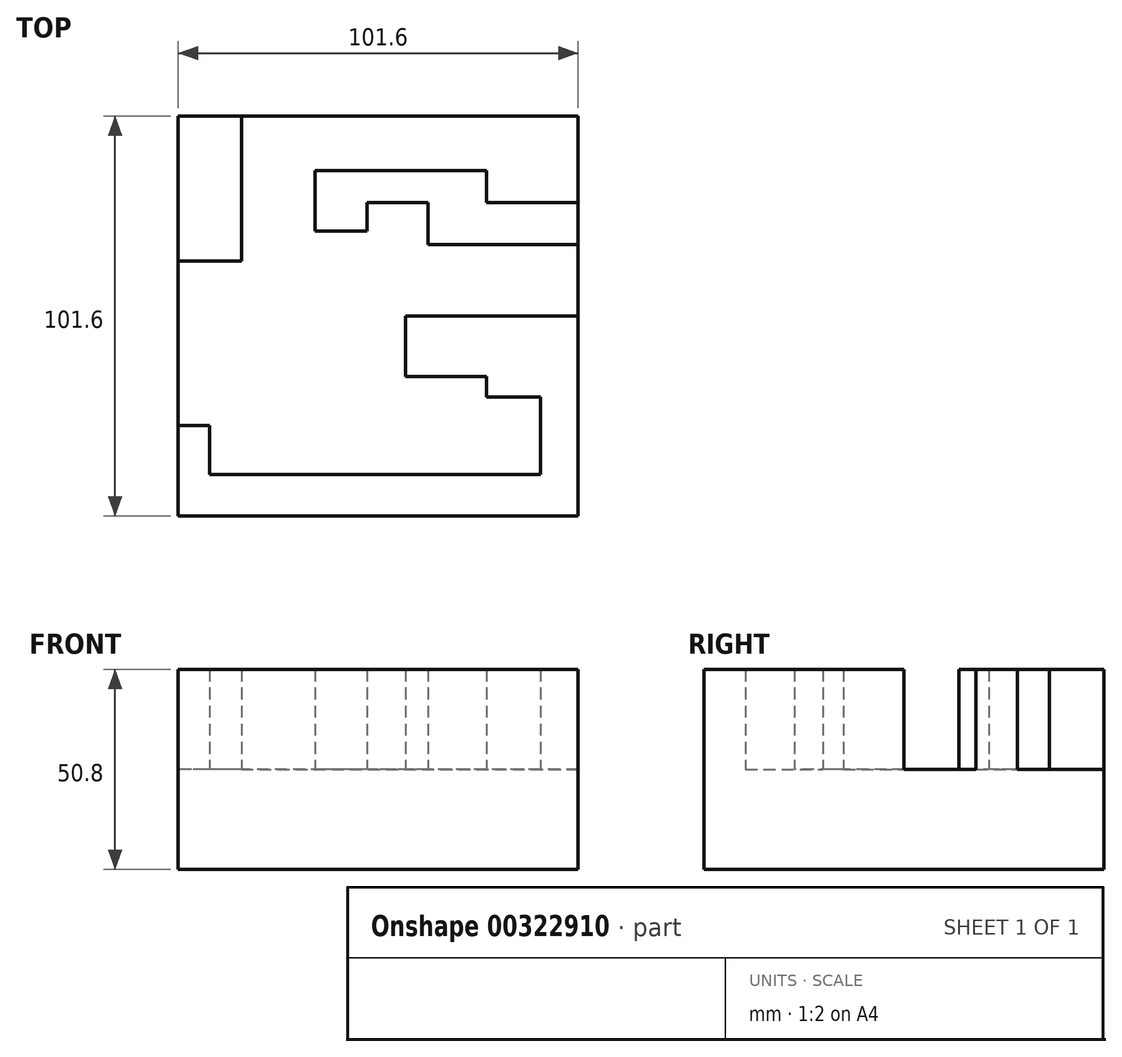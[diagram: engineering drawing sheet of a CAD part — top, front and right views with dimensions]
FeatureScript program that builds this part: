
annotation { "Feature Type Name" : "Feature", "Feature Type Description" : "" }
export const myFeature = defineFeature(function(context is Context, id is Id, definition is map)
    precondition{}
    {
        {
            var Q0;
            Q0=qCreatedBy(makeId("Top.planeOp"),FACE);
            var sketch = newSketch(context, id + "F0", { "sketchPlane" : qUnion([Q0])});
            skLineSegment(sketch, "E0.bottom", {"start": v(-47.92, 62.04) * mm, "end": v(53.68, 62.04) * mm});
            skLineSegment(sketch, "E0.top", {"start": v(-47.92, -39.56) * mm, "end": v(53.68, -39.56) * mm});
            skLineSegment(sketch, "E0.left", {"start": v(-47.92, 62.04) * mm, "end": v(-47.92, -39.56) * mm});
            skLineSegment(sketch, "E0.right", {"start": v(53.68, 62.04) * mm, "end": v(53.68, -39.56) * mm});
            skSolve(sketch);
        }
        {
            var Q0;
            Q0=makeQuery(id+"F0.imprint","IMPRINT",FACE,{"disambiguationData":[TD([[makeQuery(id+"F0.imprint","IMPRINT",EDGE,{"derivedFrom":sQuery(id+"F0.wireOp",EDGE,"E0.bottom")}),-1.0]])]});
            extrude(context, id + "F1", {"entities" : qUnion([Q0]), "depth" : 25.4 * mm});
        }
        {
            var Q0;
            Q0=makeQuery(id+"F1.opExtrude","CAP_FACE",FACE,{"disambiguationData":[OSD([sQuery(id+"F0.wireOp",EDGE,"E0.bottom"),sQuery(id+"F0.wireOp",EDGE,"E0.top"),sQuery(id+"F0.wireOp",EDGE,"E0.left"),sQuery(id+"F0.wireOp",EDGE,"E0.right")])],"isStart":false});
            var sketch = newSketch(context, id + "F2", { "sketchPlane" : qUnion([Q0])});
            skLineSegment(sketch, "E1.bottom", {"start": v(53.68, -29.03) * mm, "end": v(-8.4, -29.03) * mm});
            skLineSegment(sketch, "E1.top", {"start": v(53.68, -39.56) * mm, "end": v(-8.4, -39.56) * mm});
            skLineSegment(sketch, "E1.left", {"start": v(53.68, -29.03) * mm, "end": v(53.68, -39.56) * mm});
            skLineSegment(sketch, "E1.right", {"start": v(-8.4, -29.03) * mm, "end": v(-8.4, -39.56) * mm});
            skLineSegment(sketch, "E2.bottom", {"start": v(53.68, 29.46) * mm, "end": v(15.58, 29.46) * mm});
            skLineSegment(sketch, "E2.top", {"start": v(53.68, 40) * mm, "end": v(15.58, 40) * mm});
            skLineSegment(sketch, "E2.left", {"start": v(53.68, 29.46) * mm, "end": v(53.68, 40) * mm});
            skLineSegment(sketch, "E2.right", {"start": v(15.58, 29.46) * mm, "end": v(15.58, 40) * mm});
            skLineSegment(sketch, "E3.bottom", {"start": v(-31.88, 62.04) * mm, "end": v(-47.92, 62.04) * mm});
            skLineSegment(sketch, "E3.top", {"start": v(-31.88, 25.15) * mm, "end": v(-47.92, 25.15) * mm});
            skLineSegment(sketch, "E3.left", {"start": v(-31.88, 62.04) * mm, "end": v(-31.88, 25.15) * mm});
            skLineSegment(sketch, "E3.right", {"start": v(-47.92, 62.04) * mm, "end": v(-47.92, 25.15) * mm});
            skLineSegment(sketch, "E4.bottom", {"start": v(30.45, 40) * mm, "end": v(0, 40) * mm});
            skLineSegment(sketch, "E4.top", {"start": v(30.45, 48.16) * mm, "end": v(0, 48.16) * mm});
            skLineSegment(sketch, "E4.left", {"start": v(30.45, 40) * mm, "end": v(30.45, 48.16) * mm});
            skLineSegment(sketch, "E4.right", {"start": v(0, 40) * mm, "end": v(0, 48.16) * mm});
            skLineSegment(sketch, "E5.bottom", {"start": v(0, 48.16) * mm, "end": v(-13.18, 48.16) * mm});
            skLineSegment(sketch, "E5.top", {"start": v(0, 32.82) * mm, "end": v(-13.18, 32.82) * mm});
            skLineSegment(sketch, "E5.left", {"start": v(0, 48.16) * mm, "end": v(0, 32.82) * mm});
            skLineSegment(sketch, "E5.right", {"start": v(-13.18, 48.16) * mm, "end": v(-13.18, 32.82) * mm});
            skLineSegment(sketch, "E6.bottom", {"start": v(-39.9, 25.15) * mm, "end": v(-47.92, 25.15) * mm});
            skLineSegment(sketch, "E6.top", {"start": v(-39.9, -16.57) * mm, "end": v(-47.92, -16.57) * mm});
            skLineSegment(sketch, "E6.left", {"start": v(-39.9, 25.15) * mm, "end": v(-39.9, -16.57) * mm});
            skLineSegment(sketch, "E6.right", {"start": v(-47.92, 25.15) * mm, "end": v(-47.92, -16.57) * mm});
            skLineSegment(sketch, "E7.bottom", {"start": v(-31.88, -39.56) * mm, "end": v(-47.92, -39.56) * mm});
            skLineSegment(sketch, "E7.top", {"start": v(-31.88, -29.03) * mm, "end": v(-47.92, -29.03) * mm});
            skLineSegment(sketch, "E7.left", {"start": v(-31.88, -39.56) * mm, "end": v(-31.88, -29.03) * mm});
            skLineSegment(sketch, "E7.right", {"start": v(-47.92, -39.56) * mm, "end": v(-47.92, -29.03) * mm});
            skLineSegment(sketch, "E8.bottom", {"start": v(53.68, 11.24) * mm, "end": v(30.45, 11.24) * mm});
            skLineSegment(sketch, "E8.top", {"start": v(53.68, -9.37) * mm, "end": v(30.45, -9.37) * mm});
            skLineSegment(sketch, "E8.left", {"start": v(53.68, 11.24) * mm, "end": v(53.68, -9.37) * mm});
            skLineSegment(sketch, "E8.right", {"start": v(30.45, 11.24) * mm, "end": v(30.45, -9.37) * mm});
            skLineSegment(sketch, "E9.bottom", {"start": v(30.45, -4.1) * mm, "end": v(9.83, -4.1) * mm});
            skLineSegment(sketch, "E9.top", {"start": v(30.45, 11.24) * mm, "end": v(9.83, 11.24) * mm});
            skLineSegment(sketch, "E9.left", {"start": v(30.45, -4.1) * mm, "end": v(30.45, 11.24) * mm});
            skLineSegment(sketch, "E9.right", {"start": v(9.83, -4.1) * mm, "end": v(9.83, 11.24) * mm});
            skLineSegment(sketch, "E10.bottom", {"start": v(44.07, -29.03) * mm, "end": v(42.06, -29.03) * mm});
            skLineSegment(sketch, "E10.top", {"start": v(44.07, -9.37) * mm, "end": v(42.06, -9.37) * mm});
            skLineSegment(sketch, "E10.left", {"start": v(44.07, -29.03) * mm, "end": v(44.07, -9.37) * mm});
            skLineSegment(sketch, "E10.right", {"start": v(42.06, -29.03) * mm, "end": v(42.06, -9.37) * mm});
            skPoint(sketch, "E11.oppositeSnap0", {"position": v(42.06, 11.24) * mm});
            skLineSegment(sketch, "E11.bottom", {"start": v(42.06, 11.24) * mm, "end": v(42.06, 11.24) * mm});
            skLineSegment(sketch, "E11.top", {"start": v(42.06, 29.46) * mm, "end": v(42.06, 29.46) * mm});
            skLineSegment(sketch, "E11.left", {"start": v(42.06, 11.24) * mm, "end": v(42.06, 29.46) * mm});
            skLineSegment(sketch, "E11.right", {"start": v(42.06, 11.24) * mm, "end": v(42.06, 29.46) * mm});
            skLineSegment(sketch, "E12.bottom", {"start": v(-31.88, -39.56) * mm, "end": v(-8.4, -39.56) * mm});
            skLineSegment(sketch, "E12.top", {"start": v(-31.88, -29.03) * mm, "end": v(-8.4, -29.03) * mm});
            skLineSegment(sketch, "E12.right", {"start": v(-8.4, -39.56) * mm, "end": v(-8.4, -29.03) * mm});
            skLineSegment(sketch, "E13.bottom", {"start": v(-39.9, -29.03) * mm, "end": v(-39.9, -29.03) * mm});
            skLineSegment(sketch, "E13.top", {"start": v(-39.9, -16.57) * mm, "end": v(-39.9, -16.57) * mm});
            skLineSegment(sketch, "E13.left", {"start": v(-39.9, -29.03) * mm, "end": v(-39.9, -16.57) * mm});
            skLineSegment(sketch, "E13.right", {"start": v(-39.9, -29.03) * mm, "end": v(-39.9, -16.57) * mm});
            skLineSegment(sketch, "E14.bottom", {"start": v(-31.88, 25.15) * mm, "end": v(-8.4, 25.15) * mm});
            skLineSegment(sketch, "E14.top", {"start": v(-31.88, 10.23) * mm, "end": v(-8.4, 10.23) * mm});
            skLineSegment(sketch, "E14.left", {"start": v(-31.88, 25.15) * mm, "end": v(-31.88, 10.23) * mm});
            skLineSegment(sketch, "E14.right", {"start": v(-8.4, 25.15) * mm, "end": v(-8.4, 10.23) * mm});
            skSolve(sketch);
        }
        {
            var Q0;
            Q0=makeQuery(id+"F2.imprint","IMPRINT",FACE,{"disambiguationData":[TD([[makeQuery(id+"F2.imprint","IMPRINT",EDGE,{"derivedFrom":sQuery(id+"F2.wireOp",EDGE,"E3.bottom")}),-1.0]])]});
            var Q1;
            {var subQ3=sQuery(id+"F2.wireOp",EDGE,"E5.bottom");Q1=makeQuery(id+"F2.imprint","IMPRINT",FACE,{"disambiguationData":[TD([[makeQuery(id+"F2.imprint","IMPRINT",EDGE,{"derivedFrom":subQ3}),1.0]])]});}
            var Q2;
            {var subQ1=sQuery(id+"F2.wireOp",EDGE,"E4.top");Q2=makeQuery(id+"F2.imprint","IMPRINT",FACE,{"disambiguationData":[TD([[makeQuery(id+"F2.imprint","IMPRINT",EDGE,{"derivedFrom":subQ1}),1.0]])]});}
            var Q3;
            Q3=makeQuery(id+"F2.imprint","IMPRINT",FACE,{"disambiguationData":[TD([[makeQuery(id+"F2.imprint","IMPRINT",EDGE,{"derivedFrom":sQuery(id+"F2.wireOp",EDGE,"E2.bottom")}),-1.0]])]});
            var Q4;
            Q4=makeQuery(id+"F2.imprint","IMPRINT",FACE,{"disambiguationData":[TD([[makeQuery(id+"F2.imprint","IMPRINT",EDGE,{"derivedFrom":sQuery(id+"F2.wireOp",EDGE,"E9.bottom")}),-1.0]])]});
            var Q5;
            {var subQ3=sQuery(id+"F2.wireOp",EDGE,"E8.left");Q5=makeQuery(id+"F2.imprint","IMPRINT",FACE,{"disambiguationData":[TD([[makeQuery(id+"F2.imprint","IMPRINT",EDGE,{"derivedFrom":subQ3}),-1.0]])]});}
            var Q6;
            {var subQ3=sQuery(id+"F2.wireOp",EDGE,"E10.left");Q6=makeQuery(id+"F2.imprint","IMPRINT",FACE,{"disambiguationData":[TD([[makeQuery(id+"F2.imprint","IMPRINT",EDGE,{"derivedFrom":subQ3}),-1.0]])]});}
            var Q7;
            Q7=makeQuery(id+"F2.imprint","IMPRINT",FACE,{"disambiguationData":[TD([[makeQuery(id+"F2.imprint","IMPRINT",EDGE,{"derivedFrom":sQuery(id+"F2.wireOp",EDGE,"E1.top")}),1.0]])]});
            var Q8;
            Q8=makeQuery(id+"F2.imprint","IMPRINT",FACE,{"disambiguationData":[TD([[makeQuery(id+"F2.imprint","IMPRINT",EDGE,{"derivedFrom":sQuery(id+"F2.wireOp",EDGE,"E12.bottom")}),1.0]])]});
            var Q9;
            {var subQ0=sQuery(id+"F2.wireOp",EDGE,"E6.top");Q9=makeQuery(id+"F2.imprint","IMPRINT",FACE,{"disambiguationData":[TD([[makeQuery(id+"F2.imprint","IMPRINT",EDGE,{"derivedFrom":subQ0}),1.0]])]});}
            var Q10;
            Q10=makeQuery(id+"F2.imprint","IMPRINT",FACE,{"disambiguationData":[TD([[makeQuery(id+"F2.imprint","IMPRINT",EDGE,{"derivedFrom":sQuery(id+"F2.wireOp",EDGE,"E7.bottom")}),1.0]])]});
            var Q11;
            Q11=makeQuery(id+"F2.imprint","IMPRINT",FACE,{"disambiguationData":[TD([[makeQuery(id+"F2.imprint","IMPRINT",EDGE,{"derivedFrom":sQuery(id+"F2.wireOp",EDGE,"E6.bottom")}),1.0]])]});
            var Q12;
            {var subQ3=sQuery(id+"F2.wireOp",EDGE,"E11.right");Q12=makeQuery(id+"F2.imprint","IMPRINT",FACE,{"disambiguationData":[TD([[makeQuery(id+"F2.imprint","IMPRINT",EDGE,{"derivedFrom":subQ3}),-1.0]])]});}
            extrude(context, id + "F3", {"entities" : qUnion([Q0, Q1, Q2, Q3, Q4, Q5, Q6, Q7, Q8, Q9, Q10, Q11, Q12]), "operationType" : NewBodyOperationType.ADD, "depth" : 25.4 * mm});
        }
    });
